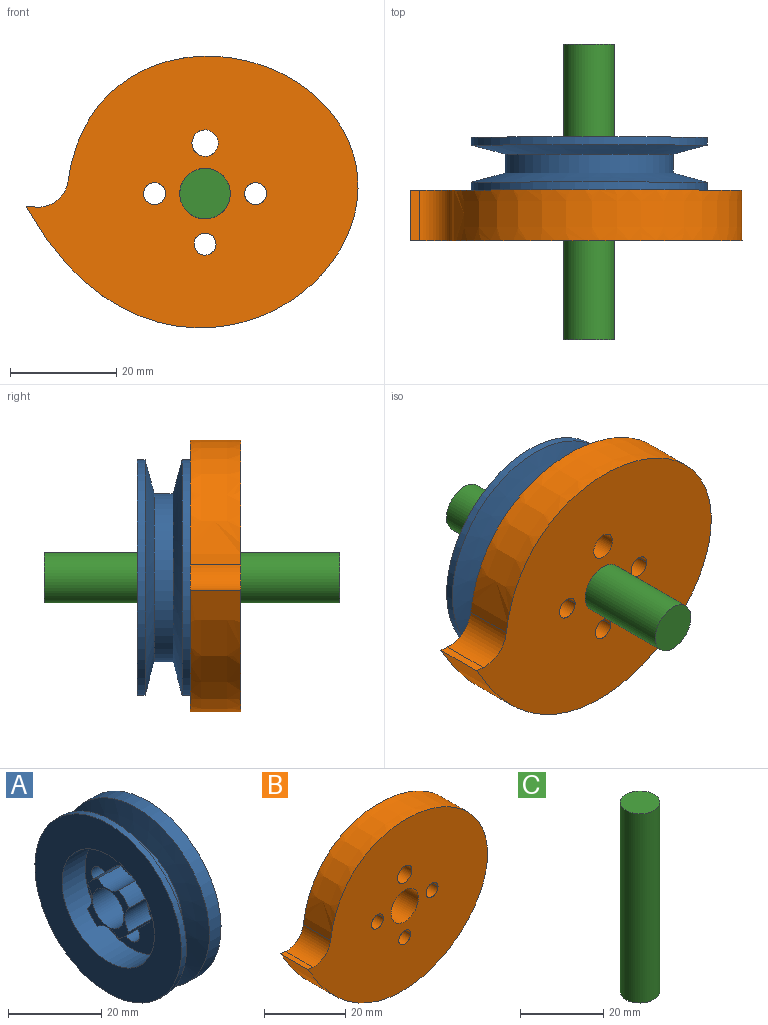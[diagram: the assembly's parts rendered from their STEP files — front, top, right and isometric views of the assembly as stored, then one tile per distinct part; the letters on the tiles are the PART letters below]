
ASSEMBLY  parts=3 mates=3
PART A: 23 faces, bbox 12x44.5x44.5 mm
  f0: plane 44.45x44.45mm, normal (-1,0,0), area 933.8mm2, adj f9,f17
  f1: cylinder r=4.5mm len=7mm, axis (-1,0,0), area 48.1mm2, adj f10,f16,f18,f19
  f2: cylinder r=4.5mm len=7mm, axis (-1,0,0), area 48.1mm2, adj f10,f16,f19,f20
  f3: cylinder r=4.5mm len=7mm, axis (-1,0,0), area 48.1mm2, adj f10,f16,f20,f21
  f4: cylinder r=4.5mm len=7mm, axis (-1,0,0), area 48.1mm2, adj f10,f16,f18,f21
  f5: cylinder r=22.23mm len=44.45mm, axis (1,0,0), area 489.8mm2, adj f6,f22
  f6: cone r=15.88mm half-angle=75deg, axis (1,0,0), area 786.9mm2, adj f5,f7
  f7: cylinder r=15.88mm len=31.75mm, axis (1,0,0), area 357.3mm2, adj f6,f8
  f8: cone r=22.23mm half-angle=75deg, axis (-1,0,0), area 786.9mm2, adj f7,f9
  f9: cylinder r=22.23mm len=44.45mm, axis (1,0,0), area 210.5mm2, adj f0,f8
  f10: plane 12.54x12.54mm, normal (-1,0,0), area 49.2mm2, adj f1,f2,f3,f4,f14,f18,f19,f20
  f11: cylinder r=2.5mm len=5mm, axis (-1,0,0), area 78.5mm2, adj f16,f22
  f12: cylinder r=2.5mm len=5mm, axis (-1,0,0), area 78.5mm2, adj f16,f22
  f13: cylinder r=2.5mm len=5mm, axis (-1,0,0), area 78.5mm2, adj f16,f22
  f14: cylinder r=4.76mm len=12mm, axis (-1,0,0), area 359.1mm2, adj f10,f22
  f15: cylinder r=2.5mm len=5mm, axis (-1,0,0), area 78.5mm2, adj f16,f22
  f16: plane 28.05x28.05mm, normal (-1,0,0), area 419mm2, adj f1,f2,f3,f4,f11,f12,f13,f15
  f17: cylinder r=14.02mm len=28.05mm, axis (-1,0,0), area 616.9mm2, adj f0,f16
  f18: cylinder r=7mm len=7mm, axis (-1,0,0), area 31.9mm2, adj f1,f4,f10,f16
  f19: cylinder r=7mm len=7mm, axis (-1,0,0), area 31.9mm2, adj f1,f2,f10,f16
  f20: cylinder r=7mm len=7mm, axis (-1,0,0), area 31.9mm2, adj f2,f3,f10,f16
  f21: cylinder r=7mm len=7mm, axis (-1,0,0), area 31.9mm2, adj f3,f4,f10,f16
  f22: plane 44.45x44.45mm, normal (1,0,0), area 1402mm2, adj f5,f11,f12,f13,f14,f15
PART B: 13 faces, bbox 62.6x9.5x51.3 mm
  f0: cylinder r=2.07mm len=9.53mm, axis (0,-1,0), area 61.9mm2, adj f1,f8,f10
  f1: cylinder r=2.07mm len=9.53mm, axis (0,-1,0), area 61.9mm2, adj f0,f8,f10
  f2: cylinder r=2.07mm len=9.53mm, axis (0,-1,0), area 61.9mm2, adj f3,f8,f10
  f3: cylinder r=2.07mm len=9.53mm, axis (0,-1,0), area 61.9mm2, adj f2,f8,f10
  f4: cylinder r=4.76mm len=9.53mm, axis (0,1,0), area 285mm2, adj f8,f10
  f5: plane 9.53x1.8mm, normal (0.09,0,1), area 17.2mm2, adj f6,f7,f8,f10
  f6: extruded ~62.62x51.17mm, area 1587.7mm2, adj f5,f7,f8,f10
  f7: cylinder r=5.71mm len=9.53mm, axis (0,1,0), area 83mm2, adj f5,f6,f8,f10
  f8: plane 62.63x51.29mm, normal (0,1,0), area 2163.5mm2, adj f0,f1,f2,f3,f4,f5,f6,f7
  f9: cylinder r=2.07mm len=9.53mm, axis (0,-1,0), area 61.9mm2, adj f8,f10,f11
  f10: plane 62.63x51.29mm, normal (0,-1,0), area 2163.5mm2, adj f0,f1,f2,f3,f4,f5,f6,f7
  f11: cylinder r=2.07mm len=9.53mm, axis (0,-1,0), area 61.9mm2, adj f8,f9,f10
  f12: cylinder r=2.5mm len=9.53mm, axis (0,-1,0), area 149.6mm2, adj f8,f10
PART C: 3 faces, bbox 9.5x9.5x55.7 mm
  f0: cylinder r=4.76mm len=55.7mm, axis (0,0,-1), area 1666.7mm2, adj f1,f2
  f1: plane 9.53x9.53mm, normal (0,0,1), area 71.3mm2, adj f0
  f2: plane 9.53x9.53mm, normal (0,0,-1), area 71.3mm2, adj f0
PLACE A rot(axis=(0.71,-0.71,0),180deg) t=(2.67,14.82,-0.38)mm
PLACE B t=(2.64,-4.7,-0.37)mm fixed
PLACE C rot(axis=(1,0,0),90deg) t=(2.64,32.33,-0.37)mm
MATE cylindrical C.f0 <-> B.f4  axis (0,1,0) through (2.64,4.48,-0.37)mm
MATE planar B.f10 <-> C.f0  axis (0,-1,0) through (-6.89,-4.7,1.7)mm
MATE cylindrical A.f5 <-> B.f8  axis (0,1,0) through (2.67,8.82,-0.38)mm
